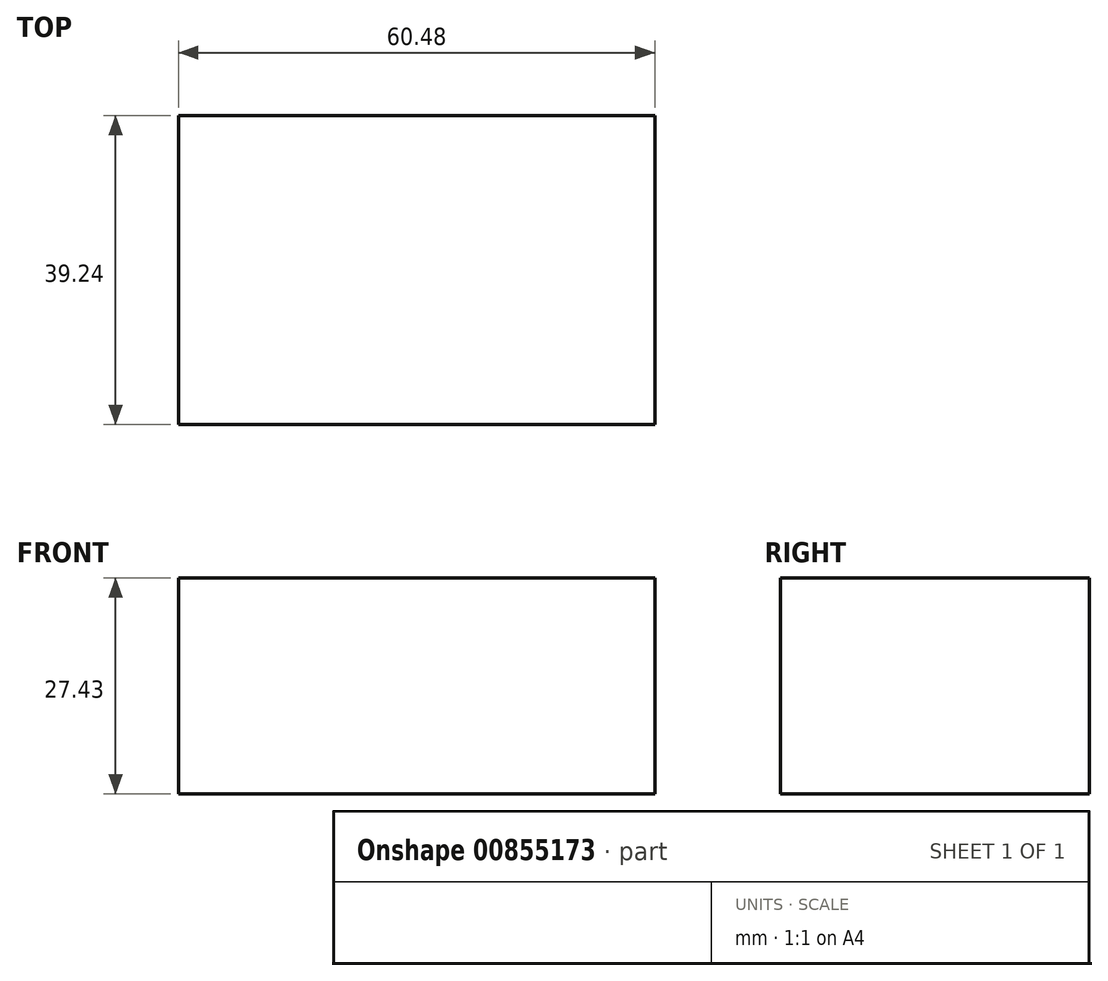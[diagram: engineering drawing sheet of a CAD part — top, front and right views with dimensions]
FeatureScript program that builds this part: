
annotation { "Feature Type Name" : "Feature", "Feature Type Description" : "" }
export const myFeature = defineFeature(function(context is Context, id is Id, definition is map)
    precondition{}
    {
        {
            var Q0;
            Q0=qCreatedBy(makeId("Top.planeOp"),FACE);
            var sketch = newSketch(context, id + "F0", { "sketchPlane" : qUnion([Q0])});
            skLineSegment(sketch, "E0.bottom", {"start": v(30.24, -19.62) * mm, "end": v(-30.24, -19.62) * mm});
            skLineSegment(sketch, "E0.top", {"start": v(30.24, 19.62) * mm, "end": v(-30.24, 19.62) * mm});
            skLineSegment(sketch, "E0.left", {"start": v(30.24, -19.62) * mm, "end": v(30.24, 19.62) * mm});
            skLineSegment(sketch, "E0.right", {"start": v(-30.24, -19.62) * mm, "end": v(-30.24, 19.62) * mm});
            skPoint(sketch, "E0.middle", {"position": v(0, 0) * mm});
            skSolve(sketch);
        }
        {
            var Q0;
            Q0 = qSketchRegion(id + "F0", true);
            extrude(context, id + "F1", {"entities" : qUnion([Q0]), "depth" : 27.43 * mm, "offsetDistance" : 25.4 * mm});
        }
    });
